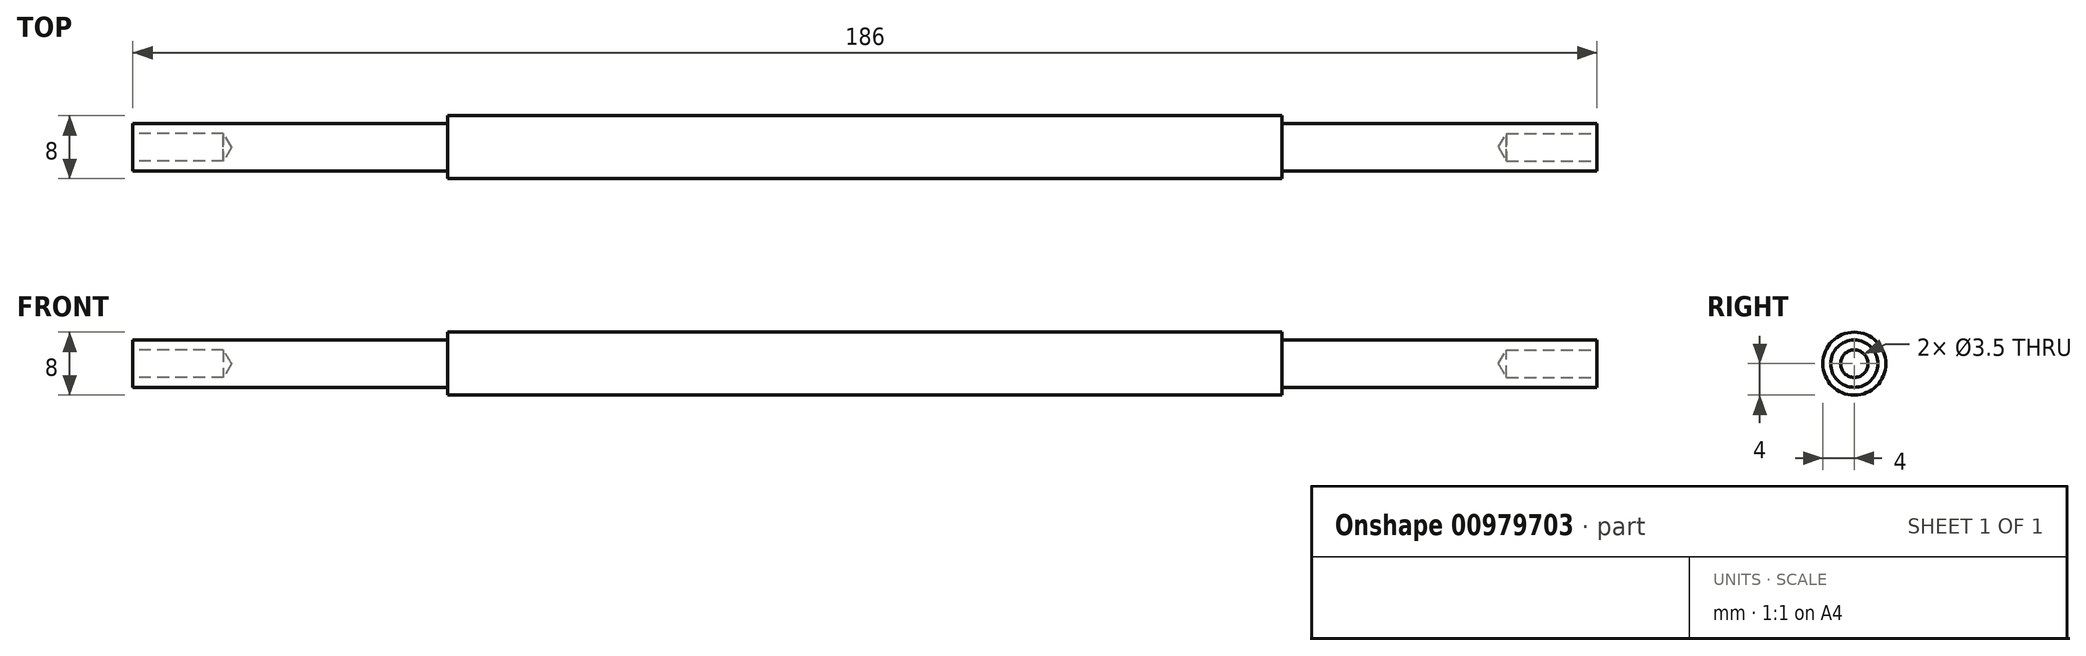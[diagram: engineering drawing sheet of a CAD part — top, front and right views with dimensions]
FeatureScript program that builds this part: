
annotation { "Feature Type Name" : "Feature", "Feature Type Description" : "" }
export const myFeature = defineFeature(function(context is Context, id is Id, definition is map)
    precondition{}
    {
        {
            var Q0;
            Q0=qCreatedBy(makeId("Front.planeOp"),FACE);
            var sketch = newSketch(context, id + "F0", { "sketchPlane" : qUnion([Q0])});
            skLineSegment(sketch, "E0.bottom", {"start": v(43, 4) * mm, "end": v(-43, 4) * mm});
            skPoint(sketch, "E0.middle", {"position": v(0, 0) * mm});
            skLineSegment(sketch, "E1", {"start": v(-53, 4) * mm, "end": v(-53, 3) * mm});
            skLineSegment(sketch, "E2", {"start": v(-53, 3) * mm, "end": v(-93, 3) * mm});
            skLineSegment(sketch, "E3", {"start": v(-93, 3) * mm, "end": v(-93, 0) * mm});
            skLineSegment(sketch, "E4", {"start": v(53, 4) * mm, "end": v(53, 3) * mm});
            skLineSegment(sketch, "E5", {"start": v(53, 3) * mm, "end": v(93, 3) * mm});
            skLineSegment(sketch, "E6", {"start": v(93, 3) * mm, "end": v(93, 0) * mm});
            skLineSegment(sketch, "E7", {"start": v(93, 0) * mm, "end": v(-93, 0) * mm});
            skLineSegment(sketch, "E8", {"start": v(-53, 4) * mm, "end": v(-43, 4) * mm});
            skLineSegment(sketch, "E9", {"start": v(43, 4) * mm, "end": v(43, 4) * mm});
            skLineSegment(sketch, "E10", {"start": v(-43, 4) * mm, "end": v(-43, 4) * mm});
            skLineSegment(sketch, "E11.trimOffspring", {"start": v(43, 4) * mm, "end": v(53, 4) * mm});
            skPoint(sketch, "E12.orphan", {"position": v(53, 4) * mm});
            skSolve(sketch);
        }
        {
            var Q0;
            Q0 = qSketchRegion(id + "F0", true);
            var Q1;
            Q1=sQuery(id+"F0.wireOp",EDGE,"E7");
            revolve(context, id + "F1", {"surfaceOperationType" : NewSurfaceOperationType.NEW, "entities" : qUnion([Q0]), "axis" : qUnion([Q1]), "revolveType" : RevolveType.FULL});
        }
        {
            var Q0;
            Q0=makeQuery(id+"F1.opRevolve","SWEPT_FACE",FACE,{"disambiguationData":[OSD([sQuery(id+"F0.wireOp",EDGE,"E3")])]});
            var sketch = newSketch(context, id + "F2", { "sketchPlane" : qUnion([Q0])});
            skPoint(sketch, "E13", {"position": v(0, 0) * mm});
            skSolve(sketch);
        }
        {
            var Q0;
            Q0=makeQuery(id+"F1.opRevolve","SWEPT_FACE",FACE,{"disambiguationData":[OSD([sQuery(id+"F0.wireOp",EDGE,"E6")])]});
            var sketch = newSketch(context, id + "F3", { "sketchPlane" : qUnion([Q0])});
            skPoint(sketch, "E14", {"position": v(0, 0) * mm});
            skSolve(sketch);
        }
        {
            var Q0;
            Q0=sQuery(id+"F3.wireOp",VERTEX,"E14");
            var Q1;
            Q1=sQuery(id+"F2.wireOp",VERTEX,"E13");
            var Q2;
            Q2=makeQuery(id+"F1.opRevolve","SWEPT_BODY",BODY,{"disambiguationData":[OSD([sQuery(id+"F0.wireOp",EDGE,"E0.bottom"),sQuery(id+"F0.wireOp",EDGE,"E1"),sQuery(id+"F0.wireOp",EDGE,"E2"),sQuery(id+"F0.wireOp",EDGE,"E3"),sQuery(id+"F0.wireOp",EDGE,"E4"),sQuery(id+"F0.wireOp",EDGE,"E5"),sQuery(id+"F0.wireOp",EDGE,"E6"),sQuery(id+"F0.wireOp",EDGE,"E7")])]});
            hole(context, id + "F4", {"style" : HoleStyle.SIMPLE, "endStyle" : HoleEndStyle.BLIND, "standardTappedOrClearance" : lookupTablePath({ "standard" : "ISO", "engagement" : "75%", "pitch" : "0.5 mm", "size" : "M4", "type" : "Tapped" }), "standardBlindInLast" : lookupTablePath({ "standard" : "ISO", "fit" : "Normal", "engagement" : "75%", "pitch" : "0.5 mm", "size" : "M4", "type" : "Clearance & tapped" }), "holeDiameter" : 3.5 * mm, "majorDiameter" : 4 * mm, "showTappedDepth" : true, "holeDepth" : 11.5 * mm, "isTappedThrough" : true, "tappedDepth" : 10 * mm, "tapClearance" : 3, "locations" : qUnion([Q0, Q1]), "scope" : qUnion([Q2])});
        }
    });
